# Revit family: xLIFE-RECSP-xx-yy Lighting_Non-Hosted_R20
name_source: partatom
category: Lighting Fixtures
units: mm (PartAtom-declared; Revit-internal decimal feet)

## family parameters
Always vertical = Yes
Cut with Voids When Loaded = No
Light Source = Yes
OmniClass Number = 23.80.70.00
OmniClass Title = Lighting
Part Type = Normal
Room Calculation Point = No
Round Connector Dimension = Use Diameter
Shared = No
Work Plane-Based = No

## types (17) — shared parameters
AS2293 Classification = C0=D50 C90=D50
Applicable Standards = AS/NZS3820, CISPR15, AS/NZS2293.3
Charging Method = Intelligent current limited constant voltage
Color Filter = 16777215
Construction = PC/ABS head
Dimensions (L x W x H) = 232mm x 51mm x 42mm (Control pack)95mm Head diameter
Dimming Lamp Color Temperature Shift = <None>
Emit Shape Visible in Rendering = No
IP Rating = IP44 (parts below ceiling) IP20 (parts above ceiling)
Lamp = Single LED (Lifetime warranty on the lamp head and loom assembly)
Manufacturer = Clevertronics
Mounting = Recessed ceiling
Operating Mode = Non-maintained
Operating Temperature = 1 ̊C to 40 ̊C
Operating Voltage = 240V AC; 50Hz
Tilt Angle = 90.00°
zero-valued in all types: Default Elevation

## per-type parameters (varying)
| type | Battery | Battery Type | Description | Emergency Lumen Output | Keynote | MIC Number | Photometric Web File | Power Consumption | Power Consumption (Standby - Lamp Off) | Replacement Battery | Replacement Emergency Driver | Replacement Emergency Lamp | Replacement Item | Testing System |
| CLIFE-RECSP | 3.2V, 3200mAh | Lithium Iron Phosphate | LP Premium Lifelight, High Performance, Recessed Emergency Light with 
IP44 Splash Proof Head, Enabled with Clevertest Plus | 224.1 lm |  | AUD02320030001 | 200250PH(CLIFE-SM-WP-HV,AS2293.3,Photometry).ies | 4.2W | 1.0W | 1550010 - Battery | AUM02370010001 CLIFE-CKIT - Driver Pack | 8050260 - LED Strip |  | Clevertest Plus Enabled (Not activated by default) |
| LLIFE-RECSP | 3.3V 2500mAh | Lithium Nanophosphate, | L10 Optimum Lifelight, High Performance, Recessed Emergency Lightwith IP44 Splash ProofHead, Enabled with Clevertest Plus | 219.6 lm |  | AUD01320020001 | LLIFE-RECSP-HV_AUD01820020001_IESA_E_LL24373A_202211301210.ies | 4.2W | 1W | 1530010 BATTERY:L10 3.3V 2.5AH 200mm lead, Brkt | AUM01370030002 LLIFE-CKIT Lifelight: LED, Control Only, L10, CTP, OWC | 8050260 LED PCA: HWSUB: CT10710-D1 |  | Clevertest Plus Enabled (Not activated by default) |
| LLIFE-RECSP-DALI-BLK | 3.3V 2500mAh | Lithium Nanophosphate, | L10 Optimum Lifelight, Recessed Emergency Light with IP44 Splash Proof Head, Black | 219.6 lm |  | AUD01210110002 | LLIFE-RECSP-HV_AUD01820020001_IESA_E_LL24373A_202211301210.ies | 4.5W | 1.3W | 1530010 - Battery | AUM01270310002 LLIFE-CKIT-DALI - Driver Pack | 8050260 - LED Strip | 8003060 - DALI Node | DALI Registered |
| LLIFE-RECSP-HVG | 3.3V 2500mAh | Lithium Nanophosphate, | Lifelight IP44 Splashproof Emergency, Recessed Mount, L10 Nanophosphate, 
Zoneworks XT Hive 2.4GHz | 219.6 lm |  | AUD01920030001 | LLIFE-RECSP-HV_AUD01820020001_IESA_E_LL24373A_202211301210.ies | 4.5W | 1.3W | 1530010 - Battery | AUM01970100001 LLIFE-CKIT-HVG - Driver Pack | 8050260 - LED Strip | 8003560 - HIVE Node | Zoneworks XT HIVE (RF) |
| LLIFE-RECSP-HV-BLK | 3.3V 2500mAh | Lithium Nanophosphate, | L10 Optimum Lifelight, Recessed Emergency Light with IP44 Splash Proof Head, 
Black | 219.6 lm |  | AUD01820060001 | LLIFE-RECSP-HV_AUD01820020001_IESA_E_LL24373A_202211301210.ies | 4.5W | 1.3W | 1530010 - Battery | AUM01870020001 LLIFE-CKIT-HV - Driver Pack | 8050250 - LED Strip | 8003191 - HIVE Node | Zoneworks XT HIVE (RF) |
| LLIFE-RECSP-ZW | 3.3V 2500mAh | Lithium Nanophosphate, | L10 Optimum Lifelight, Recessed Emergency Light with IP44 Splash Proof Head | 219.6 lm |  | AUD01120020001 | LLIFE-RECSP-HV_AUD01820020001_IESA_E_LL24373A_202211301210.ies | 4.5W | 1.3W | 1530010 - Battery | AUM01170040001 LLIFE-CKIT-ZW - Driver Pack | 8050260 - LED Strip | 8001450 - ZW Node | Zoneworks Computerised Testing |
| LLIFE-RECSP-HV | 3.3V 2500mAh | Lithium Nanophosphate, | L10 Optimum Lifelight, Recessed Emergency Light with IP44 Splash Proof Head | 219.6 lm |  | AUD01820020001 | LLIFE-RECSP-HV_AUD01820020001_IESA_E_LL24373A_202211301210.ies | 4.5W | 1.3W | 1530010 - Battery | AUM01870020001 LLIFE-CKIT-HV - Driver Pack | 8050260 - LED Strip | 8003190 - Hive Node | Zoneworks XT HIVE (RF) |
| LLIFE-RECSP-DALI | 3.3V 2500mAh | Lithium Nanophosphate, | L10 Optimum Lifelight, Recessed Emergency Light with IP44 Splash Proof Head | 219.6 lm |  | AUD01220020002 | LLIFE-RECSP-HV_AUD01820020001_IESA_E_LL24373A_202211301210.ies | 4.5W | 1.3W | 1530010 - Battery | AUM01270310002 LLIFE-CKIT-DALI - Driver Pack | 8050260 - LED Strip | 8003060 - DALI Node | DALI Registered |
| LLIFE-RECSP-BLK | 3.3V 2500mAh | Lithium Nanophosphate, | L10 Optimum Lifelight, High Performance, Recessed Emergency Light with 
IP44 Splash Proof Head, Black, Enabled with Clevertest Plus | 219.6 lm |  | AUD01320030001 | LLIFE-RECSP-HV_AUD01820020001_IESA_E_LL24373A_202211301210.ies | 4.2W | 1.0W | 1530010 - Battery | AUM01370030002 LLIFE-CKIT - Driver Pack | 8050250 - LED Strip |  | Clevertest Plus Enabled (Not activated by default) |
| CLIFE-RECSP-HV-TP | 3.2V, 3200mAh | Lithium Iron Phosphate | LP Premium Lifelight, Recessed Emergency Light with IP44 Splash Proof Head and tamperproof screws | 224.1 lm | Lifelight, LED, Rec Rnd, LP, Splash Proof, HV, TP | AUD02840020001 | 200250PH(CLIFE-SM-WP-HV,AS2293.3,Photometry).ies | 4.5W | 1.3W | 1550010 - Battery | AUM02870080001 CLIFE-CKIT-HV - Driver Pack | 8050250 - LED Strip | 8003191 - HIVE Node | Zoneworks XT HIVE (RF) |
| CLIFE-RECSP-DALI | 3.2V, 3200mAh | Lithium Iron Phosphate | LP Premium Lifelight, Recessed Emergency Light with IP44 Splash Proof Head | 224.1 lm |  | AUD02220030001 | 200250PH(CLIFE-SM-WP-HV,AS2293.3,Photometry).ies | 4.5W | 1.3W | 1550010 - Battery | AUM02270150102 CLIFE-CKIT-DALI - Driver Pack | 8050260 - LED Strip | 8003060 - DALI Node | DALI Registered |
| CLIFE-RECSP-DALI-BLK | 3.2V, 3200mAh | Lithium Iron Phosphate | LP Premium Lifelight, Recessed Emergency Light with IP44 Splash Proof Head, Black | 224.1 lm |  | AUD02210250002 | 200250PH(CLIFE-SM-WP-HV,AS2293.3,Photometry).ies | 4.5W | 1.3W | 1550010 - Battery | AUM02270150102 CLIFE-CKIT-DALI - Driver Pack | 8050260 - LED Strip | 8003060 - DALI Node | DALI Registered |
| CLIFE-RECSP-HV-BLK | 3.2V, 3200mAh | Lithium Iron Phosphate | LP Premium Lifelight, Recessed Emergency Light with IP44 Splash Proof Head, Black | 224.1 lm |  | AUD02820090001 | 200250PH(CLIFE-SM-WP-HV,AS2293.3,Photometry).ies | 4.5W | 1.3W | 1550010 - Battery | AUM02870080001 CLIFE-CKIT-HV - Driver Pack | 8050260 - LED Strip | 8003191 - HIVE Node | Zoneworks XT HIVE (RF) |
| CLIFE-RECSP-HVG | 3.2V, 3200mAh | Lithium Iron Phosphate | Lifelight IP44 Splashproof Emergency, Recessed Mount, LP,Zoneworks XT Hive 2.4GHz | 224.1 lm |  | AUD02920050001 | 200250PH(CLIFE-SM-WP-HV,AS2293.3,Photometry).ies | 4.5W | 1.3W | 1550010 - Battery | AUM02970020001 CLIFE-CKIT-HVG - Driver Pack | 8050260 - LED Strip | 8003560 - HIVE Node | Zoneworks XT HIVE (RF) |
| CLIFE-RECSP-ZW | 3.2V, 3200mAh | Lithium Iron Phosphate | LP Premium Lifelight, Recessed Emergency Light with IP44 Splash Proof Head | 224.1 lm |  | AUD02120020001 | 200250PH(CLIFE-SM-WP-HV,AS2293.3,Photometry).ies | 4.5W | 1.3W | 1550010 - Battery | AUM02170120001 CLIFE-CKIT-ZW - Driver Pack | 8050260 - LED Strip | 8001450 - HIVE Node | Zoneworks Computerised Testing |
| CLIFE-RECSP-HV | 3.2V, 3200mAh | Lithium Iron Phosphate | LP Premium Lifelight, Recessed Emergency Light with IP44 Splash Proof Head | 224.1 lm |  | AUD02820030001 | 200250PH(CLIFE-SM-WP-HV,AS2293.3,Photometry).ies | 4.5W | 1.3W | 1550010 - Battery | AUM02870080001 CLIFE-CKIT-HV - Driver Pack | 8050260 - LED Strip | 8003190 - HIVE Node | Zoneworks XT HIVE (RF) |
| CLIFE-RECSP-BLK | 3.2V, 3200mAh | Lithium Iron Phosphate | LP Premium Lifelight, High Performance, Recessed Emergency Light with 
IP44 Splash Proof Head, Black, Enabled with Clevertest Plus | 224.1 lm |  | AUD02320040001 | 200250PH(CLIFE-SM-WP-HV,AS2293.3,Photometry).ies | 4.2W | 1.0W | 1550010 - Battery | AUM02370010001 CLIFE-CKIT - Driver Pack | 8050250 - LED Strip |  | Clevertest Plus Enabled (Not activated by default) |

note: column(s) folded — value = type name in every type: Model

## geometry (parser evidence)
native form markers: Sweep x3
no freeform markers — native parametric forms only
